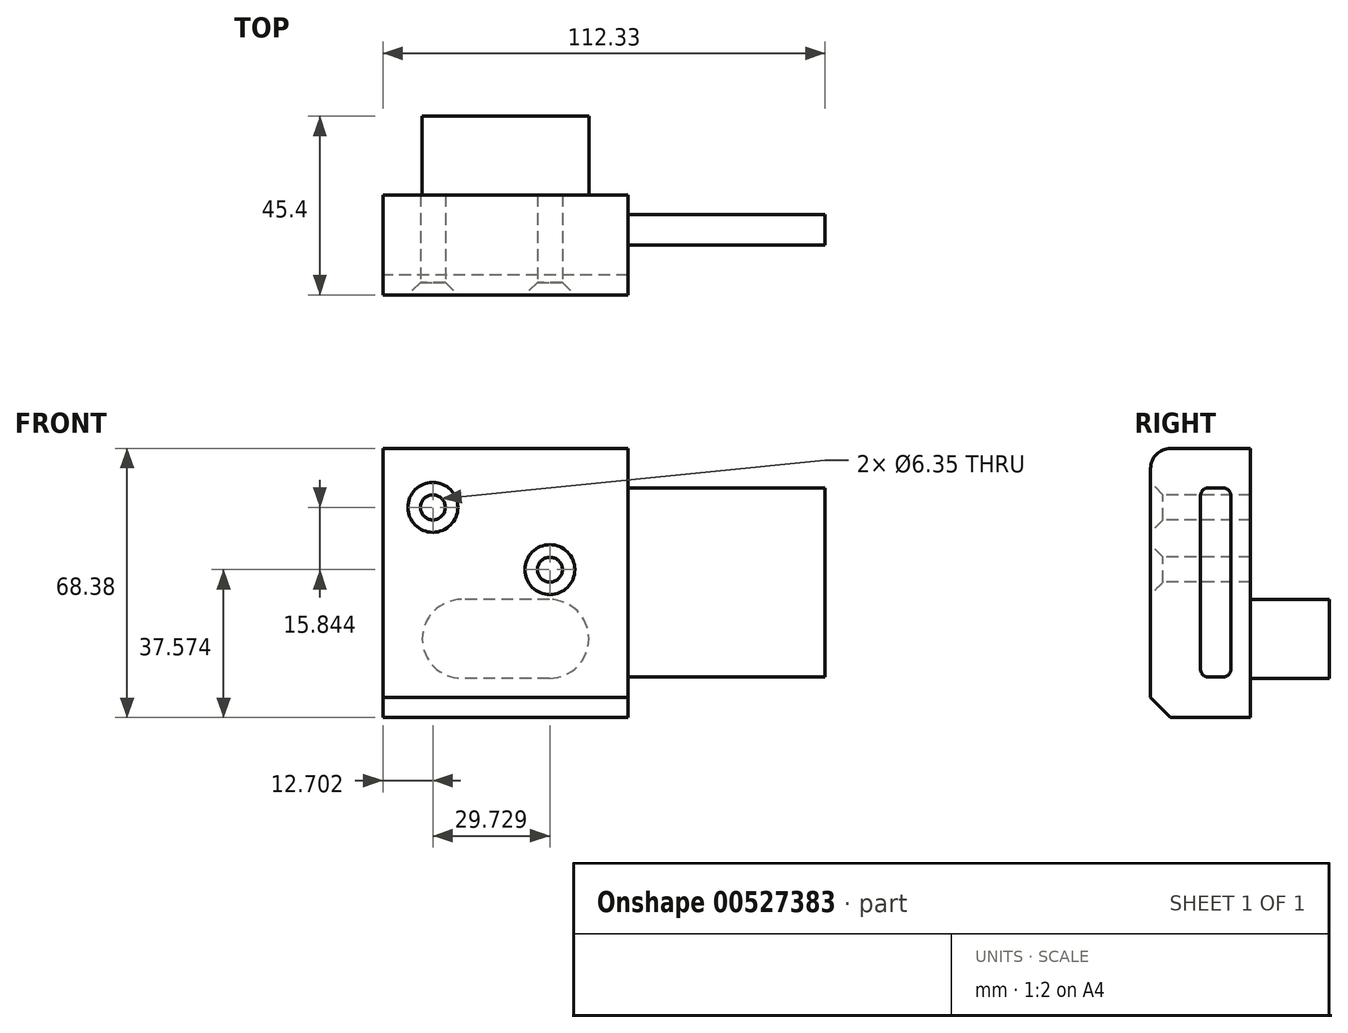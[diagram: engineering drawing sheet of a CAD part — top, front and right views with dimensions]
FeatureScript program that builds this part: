
annotation { "Feature Type Name" : "Feature", "Feature Type Description" : "" }
export const myFeature = defineFeature(function(context is Context, id is Id, definition is map)
    precondition{}
    {
        {
            var Q0;
            Q0=qCreatedBy(makeId("Front.planeOp"),FACE);
            var sketch = newSketch(context, id + "F0", { "sketchPlane" : qUnion([Q0])});
            skLineSegment(sketch, "E0.bottom", {"start": v(-67.68, 58.09) * mm, "end": v(-5.35, 58.09) * mm});
            skLineSegment(sketch, "E0.top", {"start": v(-67.68, -10.3) * mm, "end": v(-5.35, -10.3) * mm});
            skLineSegment(sketch, "E0.left", {"start": v(-67.68, 58.09) * mm, "end": v(-67.68, -10.3) * mm});
            skLineSegment(sketch, "E0.right", {"start": v(-5.35, 58.09) * mm, "end": v(-5.35, -10.3) * mm});
            skSolve(sketch);
        }
        {
            var Q0;
            Q0=makeQuery(id+"F0.imprint","IMPRINT",FACE,{"disambiguationData":[TD([[makeQuery(id+"F0.imprint","IMPRINT",EDGE,{"derivedFrom":sQuery(id+"F0.wireOp",EDGE,"E0.bottom")}),-1.0]])]});
            extrude(context, id + "F1", {"entities" : qUnion([Q0]), "endBound" : BoundingType.SYMMETRIC, "depth" : 25.4 * mm, "offsetDistance" : 25.4 * mm});
        }
        {
            var Q0;
            Q0=makeQuery(id+"F1.opExtrude","CAP_FACE",FACE,{"disambiguationData":[OSD([sQuery(id+"F0.wireOp",EDGE,"E0.bottom"),sQuery(id+"F0.wireOp",EDGE,"E0.top"),sQuery(id+"F0.wireOp",EDGE,"E0.left"),sQuery(id+"F0.wireOp",EDGE,"E0.right")])],"isStart":false});
            var sketch = newSketch(context, id + "F2", { "sketchPlane" : qUnion([Q0])});
            skPoint(sketch, "E1", {"position": v(-54.98, 43.13) * mm});
            skPoint(sketch, "E2", {"position": v(-25.25, 27.28) * mm});
            skSolve(sketch);
        }
        {
            var Q0;
            Q0=sQuery(id+"F2.wireOp",VERTEX,"E1");
            var Q1;
            Q1=sQuery(id+"F2.wireOp",VERTEX,"E2");
            var Q2;
            Q2=makeQuery(id+"F1.opExtrude","SWEPT_BODY",BODY,{"disambiguationData":[OSD([sQuery(id+"F0.wireOp",EDGE,"E0.bottom"),sQuery(id+"F0.wireOp",EDGE,"E0.top"),sQuery(id+"F0.wireOp",EDGE,"E0.left"),sQuery(id+"F0.wireOp",EDGE,"E0.right")])]});
            hole(context, id + "F3", {"style" : HoleStyle.C_SINK, "endStyle" : HoleEndStyle.THROUGH, "holeDiameter" : 6.35 * mm, "cSinkDiameter" : 12.7 * mm, "cSinkAngle" : 90 * degree, "isTappedThrough" : true, "tappedDepth" : 12.7 * mm, "tapClearance" : 3, "locations" : qUnion([Q0, Q1]), "scope" : qUnion([Q2])});
        }
        {
            var Q0;
            Q0=makeQuery(id+"F1.opExtrude","CAP_EDGE",EDGE,{"disambiguationData":[OSD([sQuery(id+"F0.wireOp",EDGE,"E0.bottom")])],"isStart":false});
            fillet(context, id + "F4", {"entities" : qUnion([Q0]), "radius" : 5.08 * mm, "tangentPropagation" : true, "allowEdgeOverflow" : false});
        }
        {
            var Q0;
            Q0=makeQuery(id+"F1.opExtrude","CAP_EDGE",EDGE,{"disambiguationData":[OSD([sQuery(id+"F0.wireOp",EDGE,"E0.top")])],"isStart":false});
            chamfer(context, id + "F5", {"entities" : qUnion([Q0]), "width" : 5.08 * mm, "tangentPropagation" : true});
        }
        {
            var Q0;
            Q0=makeQuery(id+"F1.opExtrude","CAP_FACE",FACE,{"disambiguationData":[OSD([sQuery(id+"F0.wireOp",EDGE,"E0.bottom"),sQuery(id+"F0.wireOp",EDGE,"E0.top"),sQuery(id+"F0.wireOp",EDGE,"E0.left"),sQuery(id+"F0.wireOp",EDGE,"E0.right")])],"isStart":true});
            var sketch = newSketch(context, id + "F6", { "sketchPlane" : qUnion([Q0])});
            skLineSegment(sketch, "E3.bottom", {"start": v(15.35, -0.3) * mm, "end": v(57.68, -0.3) * mm});
            skLineSegment(sketch, "E3.top", {"start": v(15.35, 19.7) * mm, "end": v(57.68, 19.7) * mm});
            skLineSegment(sketch, "E3.left", {"start": v(15.35, -0.3) * mm, "end": v(15.35, 19.7) * mm});
            skLineSegment(sketch, "E3.right", {"start": v(57.68, -0.3) * mm, "end": v(57.68, 19.7) * mm});
            skSolve(sketch);
        }
        {
            var Q0;
            Q0 = qSketchRegion(id + "F6", true);
            extrude(context, id + "F7", {"entities" : qUnion([Q0]), "operationType" : NewBodyOperationType.ADD, "depth" : 20 * mm, "offsetDistance" : 25 * mm});
        }
        {
            var Q0;
            Q0=makeQuery(id+"F7.opExtrude","SWEPT_EDGE",EDGE,{"disambiguationData":[OSD([sQuery(id+"F6.wireOp",EDGE,"E3.top"),sQuery(id+"F6.wireOp",EDGE,"E3.left")])]});
            var Q1;
            Q1=makeQuery(id+"F7.opExtrude","SWEPT_EDGE",EDGE,{"disambiguationData":[OSD([sQuery(id+"F6.wireOp",EDGE,"E3.bottom"),sQuery(id+"F6.wireOp",EDGE,"E3.left")])]});
            var Q2;
            Q2=makeQuery(id+"F7.opExtrude","SWEPT_EDGE",EDGE,{"disambiguationData":[OSD([sQuery(id+"F6.wireOp",EDGE,"E3.top"),sQuery(id+"F6.wireOp",EDGE,"E3.right")])]});
            var Q3;
            Q3=makeQuery(id+"F7.opExtrude","SWEPT_EDGE",EDGE,{"disambiguationData":[OSD([sQuery(id+"F6.wireOp",EDGE,"E3.bottom"),sQuery(id+"F6.wireOp",EDGE,"E3.right")])]});
            fillet(context, id + "F8", {"entities" : qUnion([Q0, Q1, Q2, Q3]), "radius" : 10 * mm, "tangentPropagation" : true, "allowEdgeOverflow" : false});
        }
        {
            var Q0;
            Q0=makeQuery(id+"F1.opExtrude","SWEPT_FACE",FACE,{"disambiguationData":[OSD([sQuery(id+"F0.wireOp",EDGE,"E0.right")])]});
            var sketch = newSketch(context, id + "F9", { "sketchPlane" : qUnion([Q0])});
            skLineSegment(sketch, "E4.bottom", {"start": v(0, 48.09) * mm, "end": v(7.7, 48.09) * mm});
            skLineSegment(sketch, "E4.top", {"start": v(0, 0) * mm, "end": v(7.7, 0) * mm});
            skLineSegment(sketch, "E4.left", {"start": v(0, 48.09) * mm, "end": v(0, 0) * mm});
            skLineSegment(sketch, "E4.right", {"start": v(7.7, 48.09) * mm, "end": v(7.7, 0) * mm});
            skSolve(sketch);
        }
        {
            var Q0;
            Q0=makeQuery(id+"F9.imprint","IMPRINT",FACE,{"disambiguationData":[TD([[makeQuery(id+"F9.imprint","IMPRINT",EDGE,{"derivedFrom":sQuery(id+"F9.wireOp",EDGE,"E4.bottom")}),-1.0]])]});
            extrude(context, id + "F10", {"entities" : qUnion([Q0]), "operationType" : NewBodyOperationType.ADD, "depth" : 50 * mm, "offsetDistance" : 25 * mm});
        }
        {
            var Q0;
            Q0=makeQuery(id+"F10.opExtrude","CAP_EDGE",EDGE,{"disambiguationData":[OSD([sQuery(id+"F9.wireOp",EDGE,"E4.left")])],"isStart":true});
            var Q1;
            Q1=makeQuery(id+"F10.opExtrude","CAP_EDGE",EDGE,{"disambiguationData":[OSD([sQuery(id+"F9.wireOp",EDGE,"E4.right")])],"isStart":true});
            var Q2;
            Q2=makeQuery(id+"F10.opExtrude","SWEPT_EDGE",EDGE,{"disambiguationData":[OSD([sQuery(id+"F9.wireOp",EDGE,"E4.bottom"),sQuery(id+"F9.wireOp",EDGE,"E4.right")])]});
            var Q3;
            Q3=makeQuery(id+"F10.opExtrude","SWEPT_EDGE",EDGE,{"disambiguationData":[OSD([sQuery(id+"F9.wireOp",EDGE,"E4.bottom"),sQuery(id+"F9.wireOp",EDGE,"E4.left")])]});
            var Q4;
            Q4=makeQuery(id+"F10.opExtrude","SWEPT_EDGE",EDGE,{"disambiguationData":[OSD([sQuery(id+"F9.wireOp",EDGE,"E4.top"),sQuery(id+"F9.wireOp",EDGE,"E4.right")])]});
            var Q5;
            Q5=makeQuery(id+"F10.opExtrude","SWEPT_EDGE",EDGE,{"disambiguationData":[OSD([sQuery(id+"F9.wireOp",EDGE,"E4.top"),sQuery(id+"F9.wireOp",EDGE,"E4.left")])]});
            fillet(context, id + "F11", {"entities" : qUnion([Q0, Q1, Q2, Q3, Q4, Q5]), "radius" : 2 * mm, "tangentPropagation" : true, "allowEdgeOverflow" : false});
        }
    });
